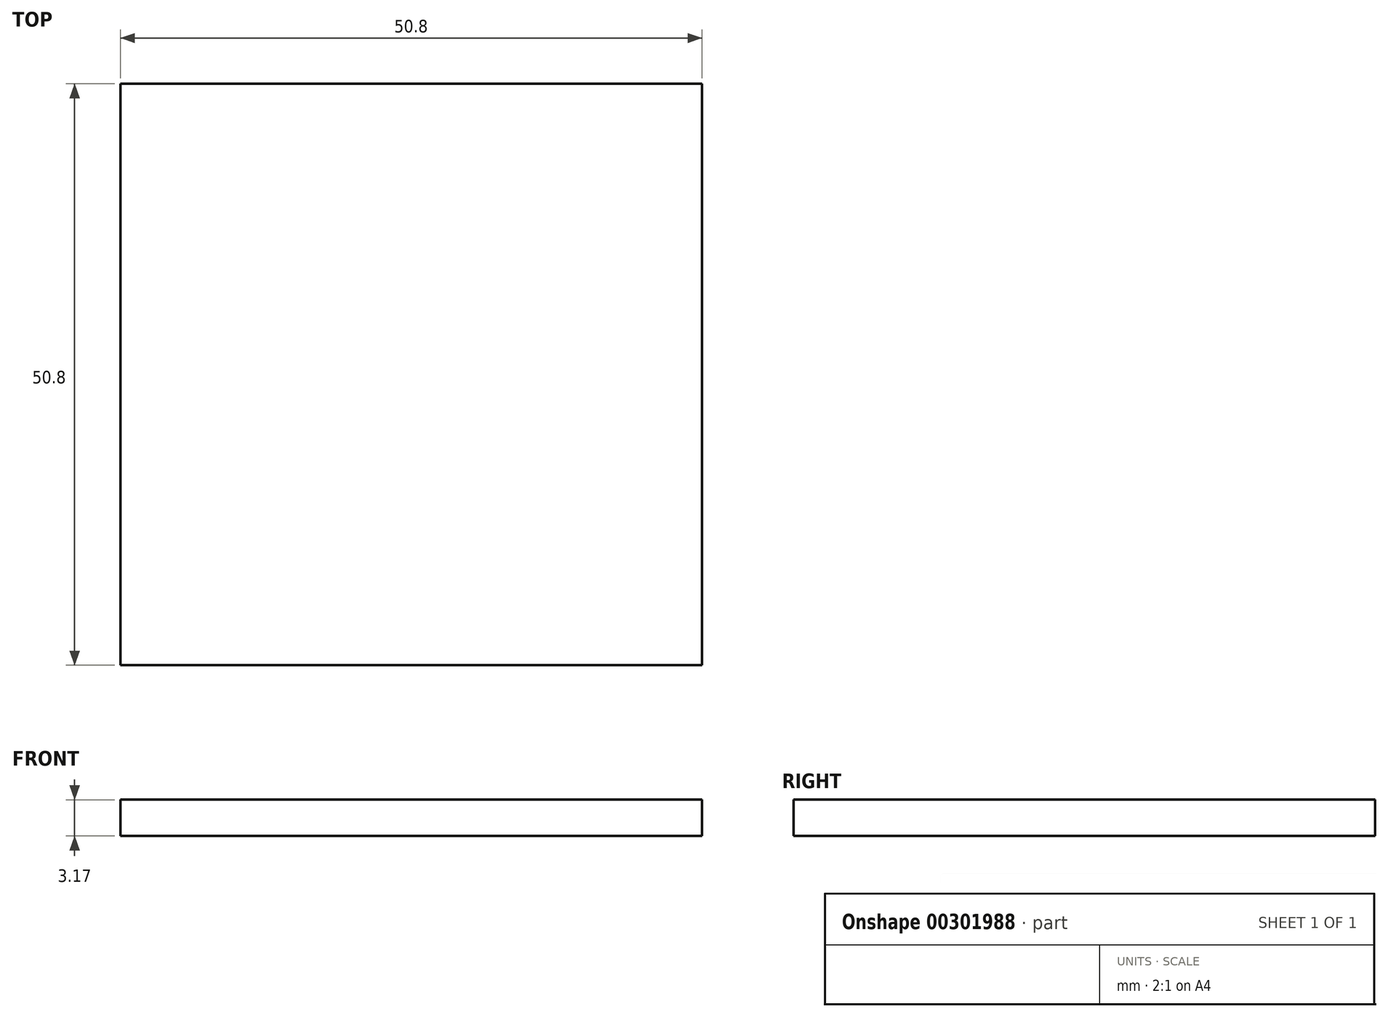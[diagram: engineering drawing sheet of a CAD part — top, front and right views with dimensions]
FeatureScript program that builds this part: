
annotation { "Feature Type Name" : "Feature", "Feature Type Description" : "" }
export const myFeature = defineFeature(function(context is Context, id is Id, definition is map)
    precondition{}
    {
        {
            var Q0;
            Q0=qCreatedBy(makeId("Top.planeOp"),FACE);
            var sketch = newSketch(context, id + "F0", { "sketchPlane" : qUnion([Q0])});
            skLineSegment(sketch, "E0.bottom", {"start": v(25.4, -25.4) * mm, "end": v(-25.4, -25.4) * mm});
            skLineSegment(sketch, "E0.top", {"start": v(25.4, 25.4) * mm, "end": v(-25.4, 25.4) * mm});
            skLineSegment(sketch, "E0.left", {"start": v(25.4, -25.4) * mm, "end": v(25.4, 25.4) * mm});
            skLineSegment(sketch, "E0.right", {"start": v(-25.4, -25.4) * mm, "end": v(-25.4, 25.4) * mm});
            skPoint(sketch, "E0.middle", {"position": v(0, 0) * mm});
            skSolve(sketch);
        }
        {
            var Q0;
            Q0=makeQuery(id+"F0.imprint","IMPRINT",FACE,{"disambiguationData":[TD([[makeQuery(id+"F0.imprint","IMPRINT",EDGE,{"derivedFrom":sQuery(id+"F0.wireOp",EDGE,"E0.bottom")}),-1.0]])]});
            extrude(context, id + "F1", {"entities" : qUnion([Q0]), "depth" : 3.17 * mm});
        }
    });
